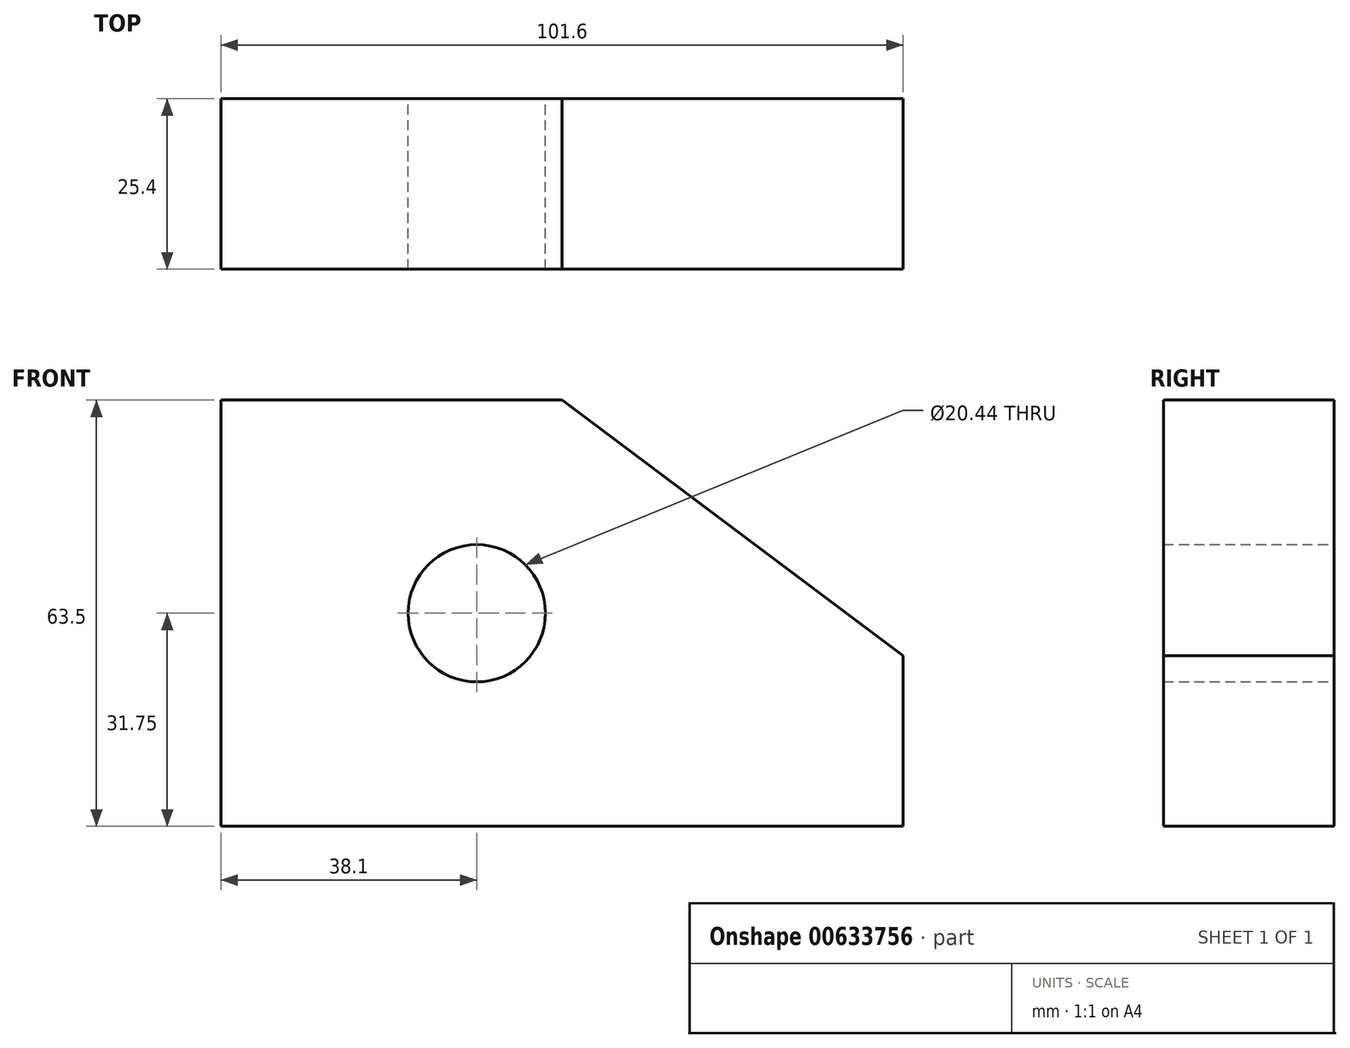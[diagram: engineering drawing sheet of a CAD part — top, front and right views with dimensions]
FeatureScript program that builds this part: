
annotation { "Feature Type Name" : "Feature", "Feature Type Description" : "" }
export const myFeature = defineFeature(function(context is Context, id is Id, definition is map)
    precondition{}
    {
        {
            var Q0;
            Q0=qCreatedBy(makeId("Front.planeOp"),FACE);
            var sketch = newSketch(context, id + "F0", { "sketchPlane" : qUnion([Q0])});
            skLineSegment(sketch, "E0", {"start": v(0, 0) * mm, "end": v(101.6, 0) * mm});
            skLineSegment(sketch, "E1", {"start": v(101.6, 0) * mm, "end": v(101.6, 25.4) * mm});
            skLineSegment(sketch, "E2", {"start": v(0, 0) * mm, "end": v(0, 63.5) * mm});
            skLineSegment(sketch, "E3", {"start": v(0, 63.5) * mm, "end": v(50.8, 63.5) * mm});
            skLineSegment(sketch, "E4", {"start": v(50.8, 63.5) * mm, "end": v(101.6, 25.4) * mm});
            skCircle(sketch, "E5", {"center": v(38.1, 31.75) * mm, "radius": 10.22 * mm});
            skSolve(sketch);
        }
        {
            var Q0;
            Q0=makeQuery(id+"F0.imprint","IMPRINT",FACE,{"disambiguationData":[TD([[makeQuery(id+"F0.imprint","IMPRINT",EDGE,{"derivedFrom":sQuery(id+"F0.wireOp",EDGE,"E0")}),1.0]])]});
            extrude(context, id + "F1", {"entities" : qUnion([Q0]), "depth" : 25.4 * mm, "offsetDistance" : 25.4 * mm});
        }
    });
